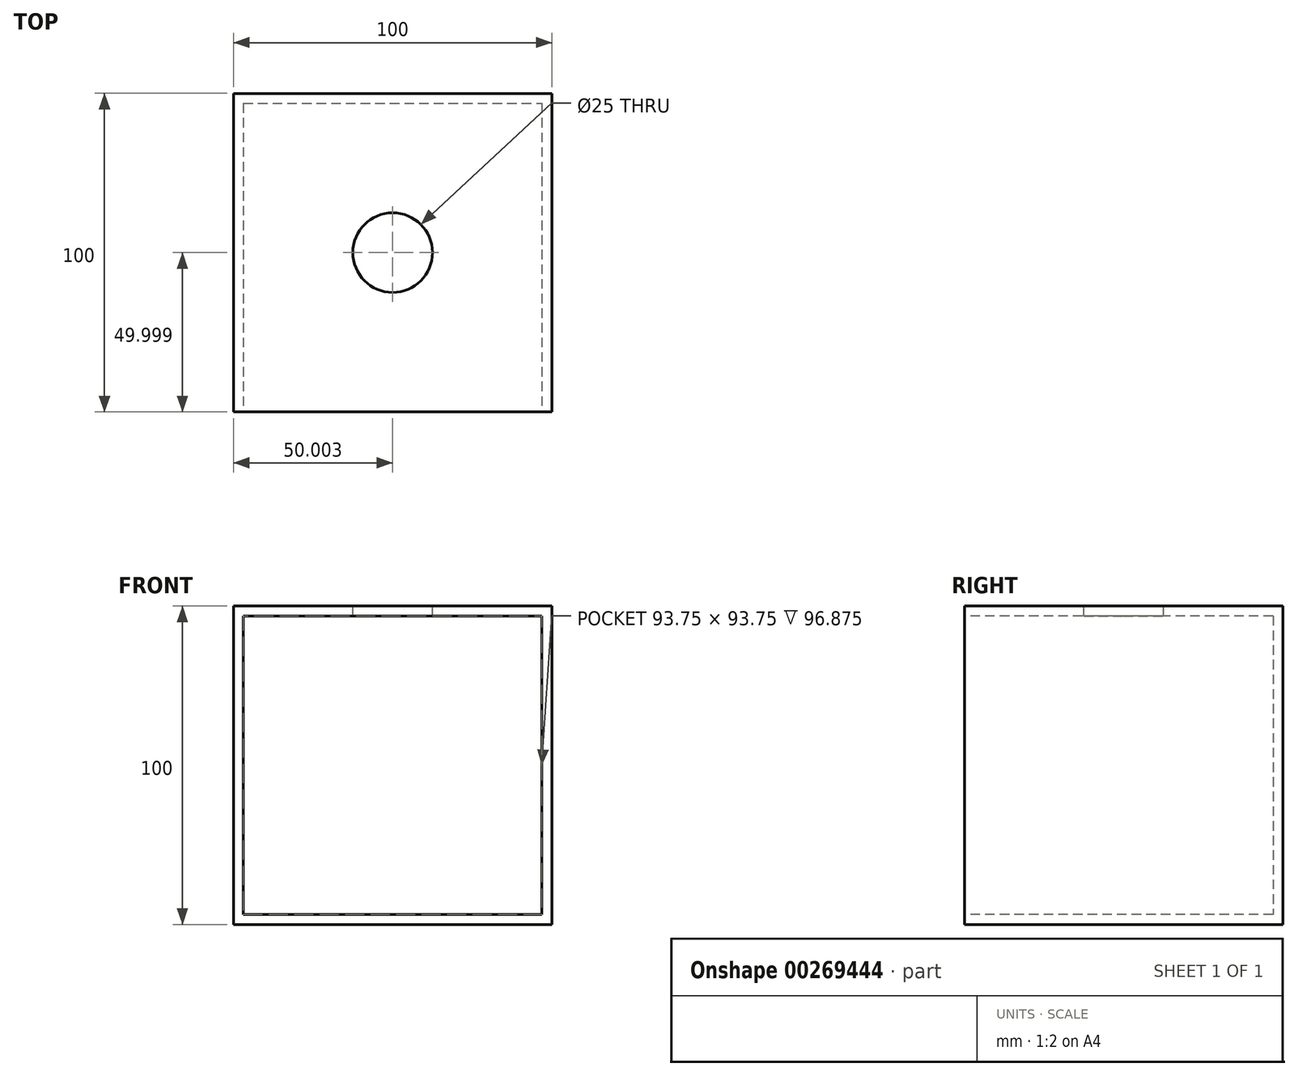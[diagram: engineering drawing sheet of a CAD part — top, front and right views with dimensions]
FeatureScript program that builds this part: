
annotation { "Feature Type Name" : "Feature", "Feature Type Description" : "" }
export const myFeature = defineFeature(function(context is Context, id is Id, definition is map)
    precondition{}
    {
        {
            var Q0;
            Q0=qCreatedBy(makeId("Top.planeOp"),FACE);
            var sketch = newSketch(context, id + "F0", { "sketchPlane" : qUnion([Q0])});
            skLineSegment(sketch, "E0.bottom", {"start": v(-54.02, 56.24) * mm, "end": v(45.98, 56.24) * mm});
            skLineSegment(sketch, "E0.top", {"start": v(-54.02, -43.76) * mm, "end": v(45.98, -43.76) * mm});
            skLineSegment(sketch, "E0.left", {"start": v(-54.02, 56.24) * mm, "end": v(-54.02, -43.76) * mm});
            skLineSegment(sketch, "E0.right", {"start": v(45.98, 56.24) * mm, "end": v(45.98, -43.76) * mm});
            skSolve(sketch);
        }
        {
            var Q0;
            Q0 = qSketchRegion(id + "F0", true);
            extrude(context, id + "F1", {"entities" : qUnion([Q0]), "depth" : 100 * mm});
        }
        {
            var Q0;
            Q0=makeQuery(id+"F1.opExtrude","SWEPT_FACE",FACE,{"disambiguationData":[OSD([sQuery(id+"F0.wireOp",EDGE,"E0.top")])]});
            shell(context, id + "F2", {"entities" : qUnion([Q0]), "thickness" : 3.12 * mm});
        }
        {
            var Q0;
            Q0=makeQuery(id+"F1.opExtrude","CAP_FACE",FACE,{"disambiguationData":[OSD([sQuery(id+"F0.wireOp",EDGE,"E0.bottom"),sQuery(id+"F0.wireOp",EDGE,"E0.top"),sQuery(id+"F0.wireOp",EDGE,"E0.left"),sQuery(id+"F0.wireOp",EDGE,"E0.right")])],"isStart":false});
            var sketch = newSketch(context, id + "F3", { "sketchPlane" : qUnion([Q0])});
            skCircle(sketch, "E1", {"center": v(-4.02, 6.24) * mm, "radius": 12.5 * mm});
            skSolve(sketch);
        }
        {
            var Q0;
            Q0=makeQuery(id+"F3.imprint","IMPRINT",FACE,{"disambiguationData":[TD([[makeQuery(id+"F3.imprint","IMPRINT",EDGE,{"derivedFrom":sQuery(id+"F3.wireOp",EDGE,"E1")}),1.0]])]});
            var Q1;
            Q1=sQuery(id+"F3.wireOp",EDGE,"E1");
            var Q2;
            {var subQ0=sQuery(id+"F0.wireOp",EDGE,"E0.right");var subQ1=sQuery(id+"F0.wireOp",EDGE,"E0.left");var subQ2=sQuery(id+"F0.wireOp",EDGE,"E0.top");var subQ3=sQuery(id+"F0.wireOp",EDGE,"E0.bottom");Q2=makeQuery(id+"F2.opShell","OFFSET_FACE",FACE,{"disambiguationData":[OSD([subQ3,subQ2,subQ1,subQ0]),TDD([makeQuery(id+"F1.opExtrude","CAP_FACE",FACE,{"disambiguationData":[OSD([subQ3,subQ2,subQ1,subQ0])],"isStart":false})])]});}
            extrude(context, id + "F4", {"entities" : qUnion([Q0]), "operationType" : NewBodyOperationType.REMOVE, "surfaceEntities" : qUnion([Q1]), "endBound" : BoundingType.UP_TO_SURFACE, "oppositeDirection" : true, "endBoundEntityFace" : qUnion([Q2]), "depth" : 18 * mm});
        }
    });
